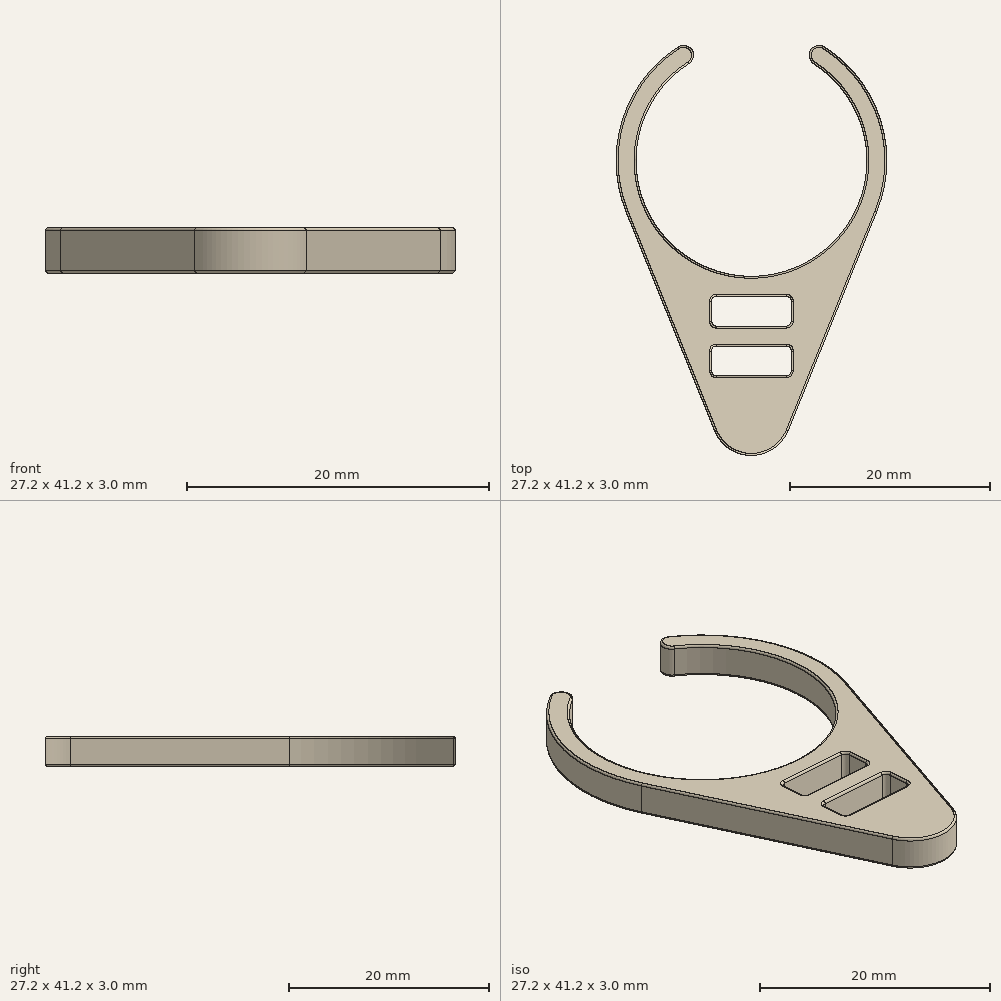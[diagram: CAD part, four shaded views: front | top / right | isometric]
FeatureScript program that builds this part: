
annotation { "Feature Type Name" : "Feature", "Feature Type Description" : "" }
export const myFeature = defineFeature(function(context is Context, id is Id, definition is map)
    precondition{}
    {
        {
            var Q0;
            Q0=qCreatedBy(makeId("Top.planeOp"),FACE);
            var sketch = newSketch(context, id + "F0", { "sketchPlane" : qUnion([Q0])});
            skCircle(sketch, "E0", {"center": v(0, 0) * mm, "radius": 13.6 * mm});
            skCircle(sketch, "E1", {"center": v(0, 0) * mm, "radius": 11.6 * mm});
            skLineSegment(sketch, "E2.bottom", {"start": v(4, -13.6) * mm, "end": v(-4, -13.6) * mm});
            skLineSegment(sketch, "E2.top", {"start": v(4, -16.6) * mm, "end": v(-4, -16.6) * mm});
            skLineSegment(sketch, "E2.left", {"start": v(4, -13.6) * mm, "end": v(4, -16.6) * mm});
            skLineSegment(sketch, "E2.right", {"start": v(-4, -13.6) * mm, "end": v(-4, -16.6) * mm});
            skPoint(sketch, "E2.middle", {"position": v(0, -15.1) * mm});
            skLineSegment(sketch, "E3.bottom", {"start": v(4, -21.6) * mm, "end": v(-4, -21.6) * mm});
            skLineSegment(sketch, "E3.top", {"start": v(4, -18.6) * mm, "end": v(-4, -18.6) * mm});
            skLineSegment(sketch, "E3.left", {"start": v(4, -21.6) * mm, "end": v(4, -18.6) * mm});
            skLineSegment(sketch, "E3.right", {"start": v(-4, -21.6) * mm, "end": v(-4, -18.6) * mm});
            skPoint(sketch, "E3.middle", {"position": v(0, -20.1) * mm});
            skCircle(sketch, "E4", {"center": v(0, -25.6) * mm, "radius": 4 * mm});
            skLineSegment(sketch, "E5", {"start": v(-12.6, -5.1) * mm, "end": v(-3.7, -27.1) * mm});
            skLineSegment(sketch, "E6", {"start": v(12.6, -5.1) * mm, "end": v(3.7, -27.1) * mm});
            skLineSegment(sketch, "E7", {"start": v(-20.8, 10.6) * mm, "end": v(21.2, 10.6) * mm});
            skCircle(sketch, "E8", {"center": v(6.81, 10.6) * mm, "radius": 1 * mm});
            skCircle(sketch, "E9", {"center": v(-6.81, 10.6) * mm, "radius": 1 * mm});
            skSolve(sketch);
        }
        {
            var Q0;
            {var subQ0=sQuery(id+"F0.wireOp",EDGE,"E4");var subQ1=makeQuery(id+"F0.imprint","INTERSECT",VERTEX,{"derivedFrom":[subQ0,sQuery(id+"F0.wireOp",EDGE,"E5")]});Q0=makeQuery(id+"F0.imprint","IMPRINT",FACE,{"disambiguationData":[TD([[makeQuery(id+"F0.imprint","IMPRINT",EDGE,{"disambiguationData":[TD([[subQ1,1.0]])],"derivedFrom":subQ0}),1.0]])]});}
            var Q1;
            {var subQ0=sQuery(id+"F0.wireOp",EDGE,"E7");var subQ1=sQuery(id+"F0.wireOp",EDGE,"E0");var subQ2=makeQuery(id+"F0.imprint","INTERSECT",VERTEX,{"disambiguationData":[OD(0.0)],"derivedFrom":[subQ1,subQ0]});Q1=makeQuery(id+"F0.imprint","IMPRINT",FACE,{"disambiguationData":[TD([[makeQuery(id+"F0.imprint","IMPRINT",EDGE,{"disambiguationData":[TD([[subQ2,-1.0]])],"derivedFrom":subQ1}),1.0]])]});}
            var Q2;
            {var subQ0=sQuery(id+"F0.wireOp",EDGE,"E7");var subQ1=sQuery(id+"F0.wireOp",EDGE,"E0");var subQ2=makeQuery(id+"F0.imprint","INTERSECT",VERTEX,{"disambiguationData":[OD(1.0)],"derivedFrom":[subQ1,subQ0]});Q2=makeQuery(id+"F0.imprint","IMPRINT",FACE,{"disambiguationData":[TD([[makeQuery(id+"F0.imprint","IMPRINT",EDGE,{"disambiguationData":[TD([[subQ2,1.0]])],"derivedFrom":subQ1}),1.0]])]});}
            var Q3;
            {var subQ0=sQuery(id+"F0.wireOp",EDGE,"E9");var subQ1=sQuery(id+"F0.wireOp",EDGE,"E7");var subQ2=makeQuery(id+"F0.imprint","INTERSECT",VERTEX,{"disambiguationData":[OD(0.0)],"derivedFrom":[subQ1,subQ0]});Q3=makeQuery(id+"F0.imprint","IMPRINT",FACE,{"disambiguationData":[TD([[makeQuery(id+"F0.imprint","IMPRINT",EDGE,{"disambiguationData":[TD([[subQ2,-1.0]])],"derivedFrom":subQ1}),1.0]])]});}
            var Q4;
            Q4=makeQuery(id+"F0.imprint","IMPRINT",FACE,{"disambiguationData":[TD([[makeQuery(id+"F0.imprint","IMPRINT",EDGE,{"derivedFrom":sQuery(id+"F0.wireOp",EDGE,"E2.top")}),1.0]])]});
            var Q5;
            {var subQ0=sQuery(id+"F0.wireOp",EDGE,"E9");var subQ1=sQuery(id+"F0.wireOp",EDGE,"E7");var subQ2=makeQuery(id+"F0.imprint","INTERSECT",VERTEX,{"disambiguationData":[OD(0.0)],"derivedFrom":[subQ1,subQ0]});Q5=makeQuery(id+"F0.imprint","IMPRINT",FACE,{"disambiguationData":[TD([[makeQuery(id+"F0.imprint","IMPRINT",EDGE,{"disambiguationData":[TD([[subQ2,-1.0]])],"derivedFrom":subQ1}),-1.0]])]});}
            var Q6;
            {var subQ0=sQuery(id+"F0.wireOp",EDGE,"E8");var subQ1=sQuery(id+"F0.wireOp",EDGE,"E7");var subQ2=makeQuery(id+"F0.imprint","INTERSECT",VERTEX,{"disambiguationData":[OD(0.0)],"derivedFrom":[subQ1,subQ0]});Q6=makeQuery(id+"F0.imprint","IMPRINT",FACE,{"disambiguationData":[TD([[makeQuery(id+"F0.imprint","IMPRINT",EDGE,{"disambiguationData":[TD([[subQ2,-1.0]])],"derivedFrom":subQ1}),-1.0]])]});}
            var Q7;
            {var subQ0=sQuery(id+"F0.wireOp",EDGE,"E8");var subQ1=sQuery(id+"F0.wireOp",EDGE,"E7");var subQ2=makeQuery(id+"F0.imprint","INTERSECT",VERTEX,{"disambiguationData":[OD(0.0)],"derivedFrom":[subQ1,subQ0]});Q7=makeQuery(id+"F0.imprint","IMPRINT",FACE,{"disambiguationData":[TD([[makeQuery(id+"F0.imprint","IMPRINT",EDGE,{"disambiguationData":[TD([[subQ2,-1.0]])],"derivedFrom":subQ1}),1.0]])]});}
            var Q8;
            {var subQ0=sQuery(id+"F0.wireOp",EDGE,"E0");var subQ9=makeQuery(id+"F0.imprint","INTERSECT",VERTEX,{"derivedFrom":[subQ0,sQuery(id+"F0.wireOp",EDGE,"E5")]});Q8=makeQuery(id+"F0.imprint","IMPRINT",FACE,{"disambiguationData":[TD([[makeQuery(id+"F0.imprint","IMPRINT",EDGE,{"disambiguationData":[TD([[subQ9,1.0]])],"derivedFrom":subQ0}),1.0]])]});}
            extrude(context, id + "F1", {"entities" : qUnion([Q0, Q1, Q2, Q3, Q4, Q5, Q6, Q7, Q8]), "endBound" : BoundingType.SYMMETRIC, "depth" : 3 * mm, "offsetDistance" : 25 * mm});
        }
        {
            var Q0;
            Q0=makeQuery(id+"F1.opExtrude","SWEPT_EDGE",EDGE,{"disambiguationData":[OSD([sQuery(id+"F0.wireOp",EDGE,"E3.top"),sQuery(id+"F0.wireOp",EDGE,"E3.right")])]});
            var Q1;
            Q1=makeQuery(id+"F1.opExtrude","SWEPT_EDGE",EDGE,{"disambiguationData":[OSD([sQuery(id+"F0.wireOp",EDGE,"E2.bottom"),sQuery(id+"F0.wireOp",EDGE,"E2.right")])]});
            var Q2;
            Q2=makeQuery(id+"F1.opExtrude","SWEPT_EDGE",EDGE,{"disambiguationData":[OSD([sQuery(id+"F0.wireOp",EDGE,"E2.top"),sQuery(id+"F0.wireOp",EDGE,"E2.right")])]});
            var Q3;
            Q3=makeQuery(id+"F1.opExtrude","SWEPT_EDGE",EDGE,{"disambiguationData":[OSD([sQuery(id+"F0.wireOp",EDGE,"E3.bottom"),sQuery(id+"F0.wireOp",EDGE,"E3.right")])]});
            var Q4;
            Q4=makeQuery(id+"F1.opExtrude","SWEPT_EDGE",EDGE,{"disambiguationData":[OSD([sQuery(id+"F0.wireOp",EDGE,"E3.bottom"),sQuery(id+"F0.wireOp",EDGE,"E3.left")])]});
            var Q5;
            Q5=makeQuery(id+"F1.opExtrude","SWEPT_EDGE",EDGE,{"disambiguationData":[OSD([sQuery(id+"F0.wireOp",EDGE,"E2.top"),sQuery(id+"F0.wireOp",EDGE,"E2.left")])]});
            var Q6;
            Q6=makeQuery(id+"F1.opExtrude","SWEPT_EDGE",EDGE,{"disambiguationData":[OSD([sQuery(id+"F0.wireOp",EDGE,"E2.bottom"),sQuery(id+"F0.wireOp",EDGE,"E2.left")])]});
            var Q7;
            Q7=makeQuery(id+"F1.opExtrude","SWEPT_EDGE",EDGE,{"disambiguationData":[OSD([sQuery(id+"F0.wireOp",EDGE,"E3.top"),sQuery(id+"F0.wireOp",EDGE,"E3.left")])]});
            fillet(context, id + "F2", {"entities" : qUnion([Q0, Q1, Q2, Q3, Q4, Q5, Q6, Q7]), "radius" : 0.5 * mm, "tangentPropagation" : true, "allowEdgeOverflow" : false});
        }
        {
            var Q0;
            Q0=makeQuery(id+"F1.opExtrude","CAP_FACE",FACE,{"disambiguationData":[OSD([sQuery(id+"F0.wireOp",EDGE,"E0"),sQuery(id+"F0.wireOp",EDGE,"E1"),sQuery(id+"F0.wireOp",EDGE,"E2.bottom"),sQuery(id+"F0.wireOp",EDGE,"E2.top"),sQuery(id+"F0.wireOp",EDGE,"E2.left"),sQuery(id+"F0.wireOp",EDGE,"E2.right"),sQuery(id+"F0.wireOp",EDGE,"E3.bottom"),sQuery(id+"F0.wireOp",EDGE,"E3.top"),sQuery(id+"F0.wireOp",EDGE,"E3.left"),sQuery(id+"F0.wireOp",EDGE,"E3.right"),sQuery(id+"F0.wireOp",EDGE,"E4"),sQuery(id+"F0.wireOp",EDGE,"E5"),sQuery(id+"F0.wireOp",EDGE,"E6"),sQuery(id+"F0.wireOp",EDGE,"E8"),sQuery(id+"F0.wireOp",EDGE,"E9")])],"isStart":false});
            var Q1;
            Q1=makeQuery(id+"F1.opExtrude","CAP_FACE",FACE,{"disambiguationData":[OSD([sQuery(id+"F0.wireOp",EDGE,"E0"),sQuery(id+"F0.wireOp",EDGE,"E1"),sQuery(id+"F0.wireOp",EDGE,"E2.bottom"),sQuery(id+"F0.wireOp",EDGE,"E2.top"),sQuery(id+"F0.wireOp",EDGE,"E2.left"),sQuery(id+"F0.wireOp",EDGE,"E2.right"),sQuery(id+"F0.wireOp",EDGE,"E3.bottom"),sQuery(id+"F0.wireOp",EDGE,"E3.top"),sQuery(id+"F0.wireOp",EDGE,"E3.left"),sQuery(id+"F0.wireOp",EDGE,"E3.right"),sQuery(id+"F0.wireOp",EDGE,"E4"),sQuery(id+"F0.wireOp",EDGE,"E5"),sQuery(id+"F0.wireOp",EDGE,"E6"),sQuery(id+"F0.wireOp",EDGE,"E8"),sQuery(id+"F0.wireOp",EDGE,"E9")])],"isStart":true});
            fillet(context, id + "F3", {"entities" : qUnion([Q0, Q1]), "radius" : 0.2 * mm, "tangentPropagation" : true, "allowEdgeOverflow" : false});
        }
    });
